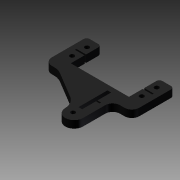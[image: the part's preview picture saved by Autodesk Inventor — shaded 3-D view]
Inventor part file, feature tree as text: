
AUTODESK INVENTOR PART (.ipt)
format: ipt  version: 2012 (Build 160160000, 160)  size: 135,168 bytes
history: native  units: mm
features: extrude x1, sketch x1
ambient origin geometry x8: Origin, YZ Plane, XZ Plane, XY Plane, X Axis, Y Axis, Z Axis, Center Point
bodies: Solid1 (feature_tree)
feature tree (2):
  extrude  "Extrusion1"  Depth=1.25mm
  sketch  "Sketch1"  dims[d8=19.85mm d13=1.25mm d15=2.5mm d16=19.8mm d17=5.0mm d20=1.25mm d25=9.4mm d26=2.5mm d27=1.0mm d28=1.0mm d29=1.0mm d30=6.5mm d48=5.0mm d54=10.0mm d57=10.0mm d58=2.0mm d59=5.0mm d60=0.0mm]
